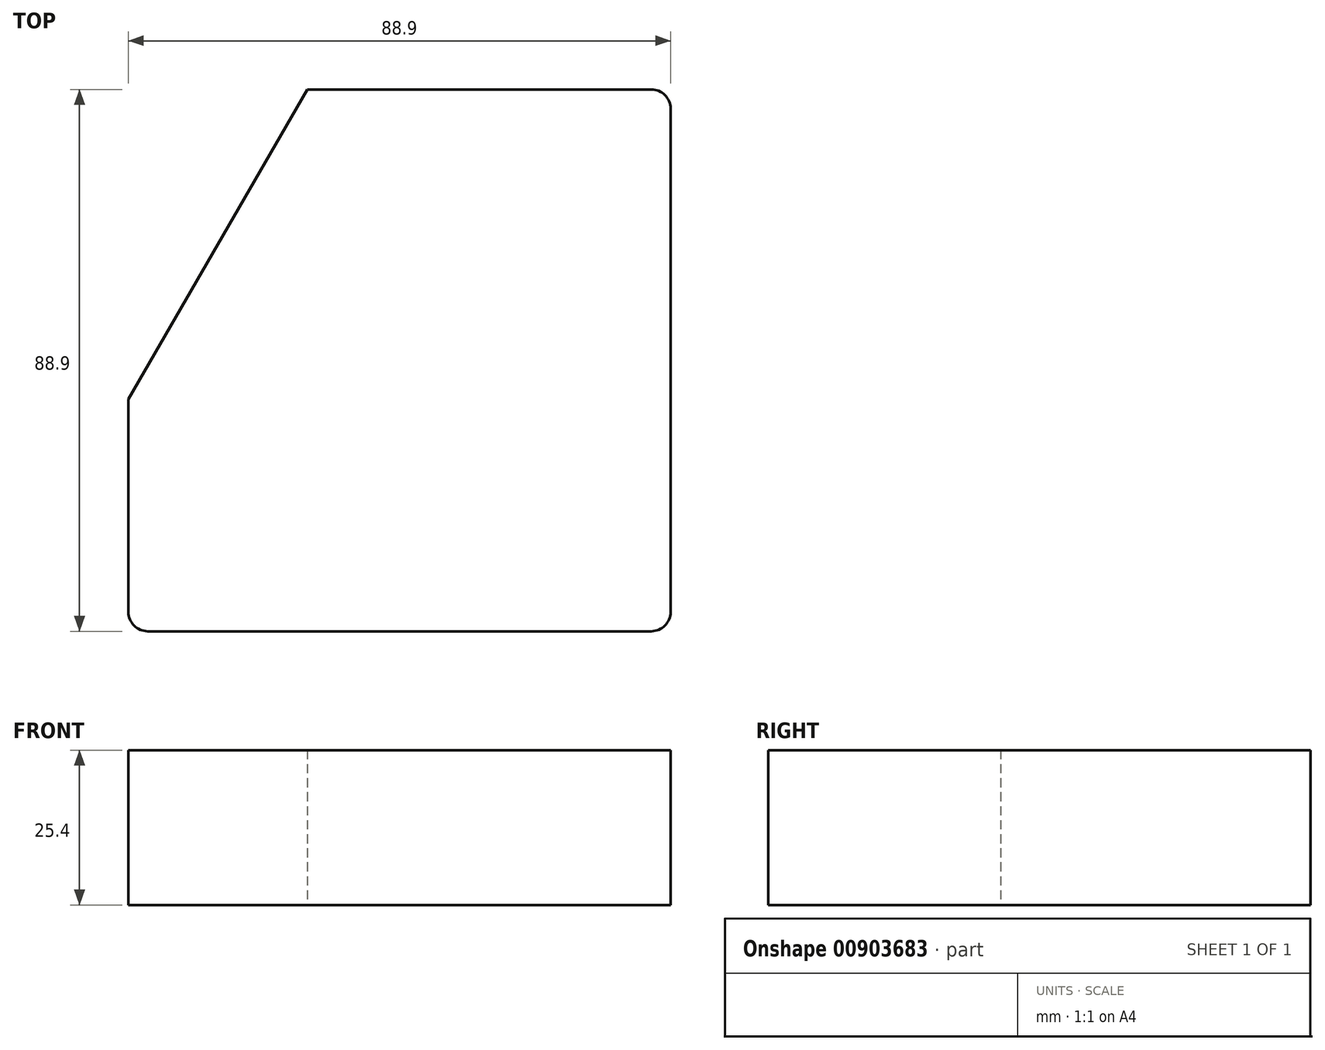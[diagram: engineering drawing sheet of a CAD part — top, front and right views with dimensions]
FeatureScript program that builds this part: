
annotation { "Feature Type Name" : "Feature", "Feature Type Description" : "" }
export const myFeature = defineFeature(function(context is Context, id is Id, definition is map)
    precondition{}
    {
        {
            var Q0;
            Q0=qCreatedBy(makeId("Top.planeOp"),FACE);
            var sketch = newSketch(context, id + "F0", { "sketchPlane" : qUnion([Q0])});
            skLineSegment(sketch, "E0.bottom", {"start": v(41.28, 44.45) * mm, "end": v(-41.27, 44.45) * mm});
            skLineSegment(sketch, "E0.top", {"start": v(41.28, -44.45) * mm, "end": v(-41.28, -44.45) * mm});
            skLineSegment(sketch, "E0.left", {"start": v(44.45, 41.28) * mm, "end": v(44.45, -41.28) * mm});
            skLineSegment(sketch, "E0.right", {"start": v(-44.45, 41.28) * mm, "end": v(-44.45, -41.28) * mm});
            skPoint(sketch, "E0.middle", {"position": v(0, 0) * mm});
            skPoint(sketch, "E1.visualSharp", {"position": v(-44.45, 44.45) * mm});
            skArc(sketch, "E1.filletArc", {"start": v(-41.27, 44.45) * mm, "mid": v(-43.52, 43.52) * mm, "end": v(-44.45, 41.28) * mm});
            skPoint(sketch, "E2.visualSharp", {"position": v(44.45, 44.45) * mm});
            skArc(sketch, "E2.filletArc", {"start": v(44.45, 41.28) * mm, "mid": v(43.52, 43.52) * mm, "end": v(41.28, 44.45) * mm});
            skPoint(sketch, "E3.visualSharp", {"position": v(44.45, -44.45) * mm});
            skArc(sketch, "E3.filletArc", {"start": v(41.28, -44.45) * mm, "mid": v(43.52, -43.52) * mm, "end": v(44.45, -41.28) * mm});
            skPoint(sketch, "E4.visualSharp", {"position": v(-44.45, -44.45) * mm});
            skArc(sketch, "E4.filletArc", {"start": v(-44.45, -41.28) * mm, "mid": v(-43.52, -43.52) * mm, "end": v(-41.28, -44.45) * mm});
            skLineSegment(sketch, "E5", {"start": v(-15.12, 44.45) * mm, "end": v(-44.45, -6.35) * mm});
            skSolve(sketch);
        }
        {
            var Q0;
            Q0=makeQuery(id+"F0.imprint","IMPRINT",FACE,{"disambiguationData":[TD([[makeQuery(id+"F0.imprint","IMPRINT",EDGE,{"derivedFrom":sQuery(id+"F0.wireOp",EDGE,"E0.top")}),-1.0]])]});
            extrude(context, id + "F1", {"entities" : qUnion([Q0]), "depth" : 25.4 * mm, "offsetDistance" : 25.4 * mm});
        }
    });
